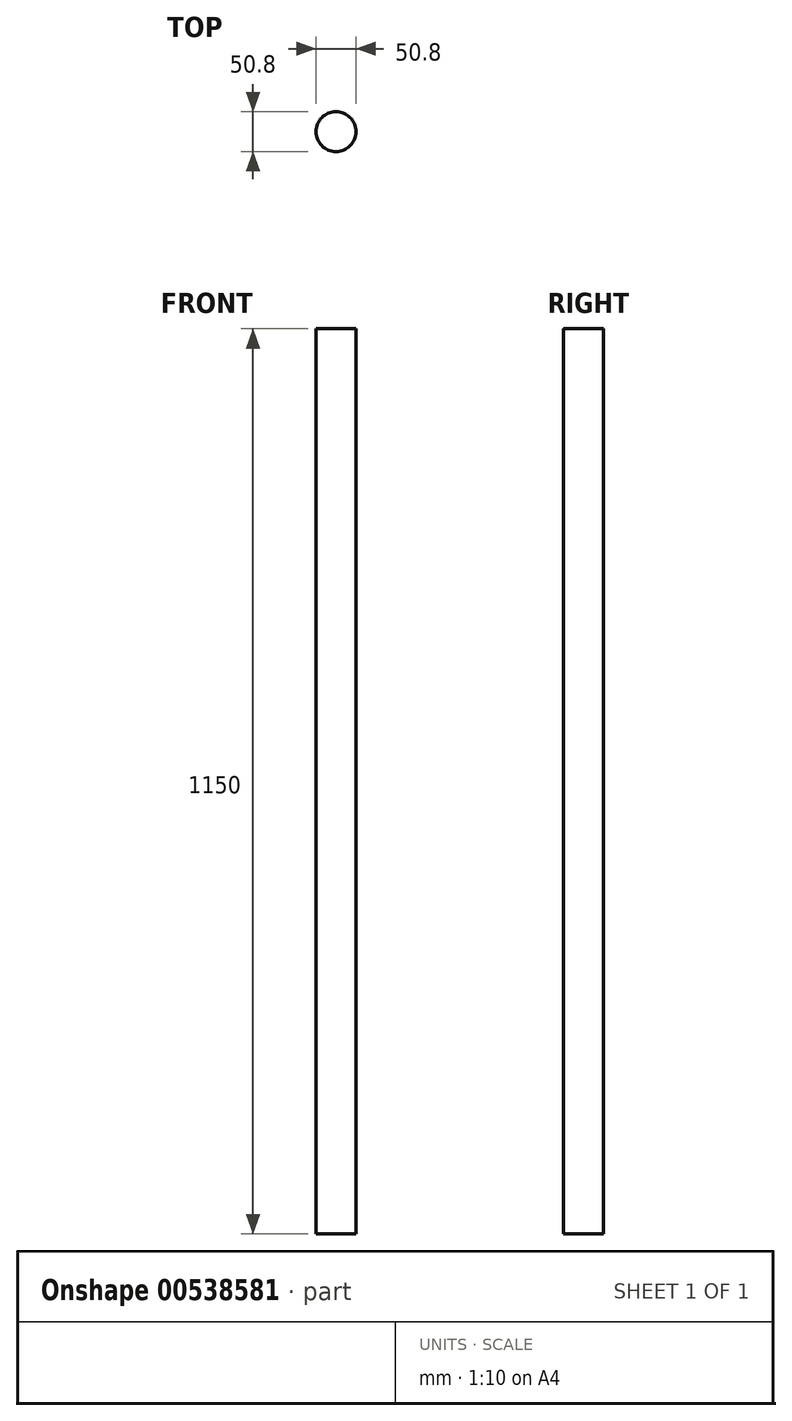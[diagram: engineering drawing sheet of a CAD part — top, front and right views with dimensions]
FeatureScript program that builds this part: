
annotation { "Feature Type Name" : "Feature", "Feature Type Description" : "" }
export const myFeature = defineFeature(function(context is Context, id is Id, definition is map)
    precondition{}
    {
        {
            var Q0;
            Q0=qCreatedBy(makeId("Top.planeOp"),FACE);
            var sketch = newSketch(context, id + "F0", { "sketchPlane" : qUnion([Q0])});
            skCircle(sketch, "E0", {"center": v(0, 0) * mm, "radius": 25.4 * mm});
            skSolve(sketch);
        }
        {
            var Q0;
            Q0 = qSketchRegion(id + "F0", true);
            extrude(context, id + "F1", {"entities" : qUnion([Q0]), "depth" : 1150 * mm, "offsetDistance" : 25 * mm});
        }
    });
